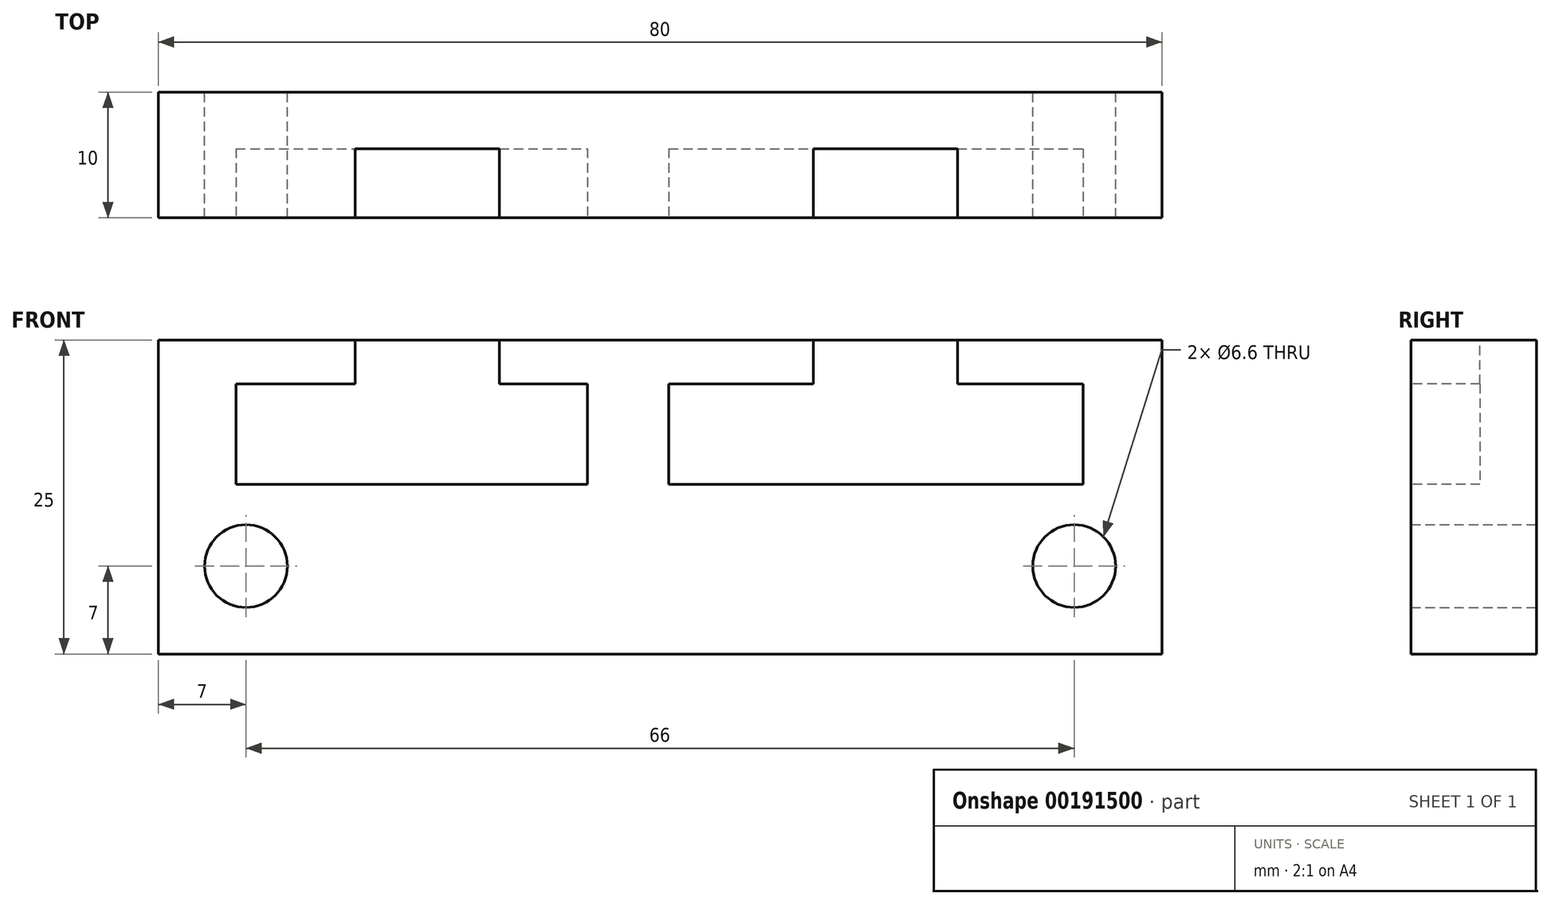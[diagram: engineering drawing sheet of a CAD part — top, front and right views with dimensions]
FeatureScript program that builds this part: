
annotation { "Feature Type Name" : "Feature", "Feature Type Description" : "" }
export const myFeature = defineFeature(function(context is Context, id is Id, definition is map)
    precondition{}
    {
        {
            var Q0;
            Q0=qCreatedBy(makeId("Front.planeOp"),FACE);
            var sketch = newSketch(context, id + "F0", { "sketchPlane" : qUnion([Q0])});
            skLineSegment(sketch, "E0.bottom", {"start": v(0, 0) * mm, "end": v(80, 0) * mm});
            skLineSegment(sketch, "E0.top", {"start": v(0, 25) * mm, "end": v(80, 25) * mm});
            skLineSegment(sketch, "E0.left", {"start": v(0, 0) * mm, "end": v(0, 25) * mm});
            skLineSegment(sketch, "E0.right", {"start": v(80, 0) * mm, "end": v(80, 25) * mm});
            skLineSegment(sketch, "E1.bottom", {"start": v(0, 0) * mm, "end": v(7, 0) * mm, "construction": true});
            skLineSegment(sketch, "E1.top", {"start": v(0, 7) * mm, "end": v(7, 7) * mm, "construction": true});
            skLineSegment(sketch, "E1.left", {"start": v(0, 0) * mm, "end": v(0, 7) * mm, "construction": true});
            skLineSegment(sketch, "E1.right", {"start": v(7, 0) * mm, "end": v(7, 7) * mm, "construction": true});
            skLineSegment(sketch, "E2.bottom", {"start": v(80, 0) * mm, "end": v(73, 0) * mm, "construction": true});
            skLineSegment(sketch, "E2.top", {"start": v(80, 7) * mm, "end": v(73, 7) * mm, "construction": true});
            skLineSegment(sketch, "E2.left", {"start": v(80, 0) * mm, "end": v(80, 7) * mm, "construction": true});
            skLineSegment(sketch, "E2.right", {"start": v(73, 0) * mm, "end": v(73, 7) * mm, "construction": true});
            skCircle(sketch, "E3", {"center": v(7, 7) * mm, "radius": 3.3 * mm});
            skCircle(sketch, "E4", {"center": v(73, 7) * mm, "radius": 3.3 * mm});
            skSolve(sketch);
        }
        {
            var Q0;
            Q0=makeQuery(id+"F0.imprint","IMPRINT",FACE,{"disambiguationData":[TD([[makeQuery(id+"F0.imprint","IMPRINT",EDGE,{"derivedFrom":sQuery(id+"F0.wireOp",EDGE,"E0.bottom")}),1.0]])]});
            extrude(context, id + "F1", {"entities" : qUnion([Q0]), "depth" : 10 * mm});
        }
        {
            var Q0;
            Q0=makeQuery(id+"F1.opExtrude","CAP_FACE",FACE,{"disambiguationData":[OSD([sQuery(id+"F0.wireOp",EDGE,"E0.bottom"),sQuery(id+"F0.wireOp",EDGE,"E0.top"),sQuery(id+"F0.wireOp",EDGE,"E0.left"),sQuery(id+"F0.wireOp",EDGE,"E0.right")])],"isStart":false});
            var sketch = newSketch(context, id + "F2", { "sketchPlane" : qUnion([Q0])});
            skPoint(sketch, "E5.bottom.start.orphan", {"position": v(0, 21.5) * mm});
            skPoint(sketch, "E6.end.orphan", {"position": v(80, 21.5) * mm});
            skPoint(sketch, "E7.start.orphan", {"position": v(16.7, 21.5) * mm});
            skPoint(sketch, "E8.start.orphan", {"position": v(28.2, 21.5) * mm});
            skPoint(sketch, "E9.end.orphan", {"position": v(55.3, 21.5) * mm});
            skPoint(sketch, "E10.start.orphan", {"position": v(66.8, 21.5) * mm});
            skLineSegment(sketch, "E11", {"start": v(0, 21.5) * mm, "end": v(6.2, 21.5) * mm, "construction": true});
            skLineSegment(sketch, "E12", {"start": v(6.2, 21.5) * mm, "end": v(15.7, 21.5) * mm});
            skLineSegment(sketch, "E13", {"start": v(15.7, 21.5) * mm, "end": v(15.7, 25) * mm});
            skLineSegment(sketch, "E14", {"start": v(15.7, 25) * mm, "end": v(27.2, 25) * mm});
            skLineSegment(sketch, "E15", {"start": v(27.2, 25) * mm, "end": v(27.2, 21.5) * mm});
            skLineSegment(sketch, "E16", {"start": v(27.2, 21.5) * mm, "end": v(34.2, 21.5) * mm});
            skLineSegment(sketch, "E17", {"start": v(34.2, 21.5) * mm, "end": v(40.7, 21.5) * mm, "construction": true});
            skLineSegment(sketch, "E18", {"start": v(40.7, 21.5) * mm, "end": v(52.2, 21.5) * mm});
            skLineSegment(sketch, "E19", {"start": v(52.2, 21.5) * mm, "end": v(52.2, 25) * mm});
            skLineSegment(sketch, "E20", {"start": v(52.2, 25) * mm, "end": v(63.7, 25) * mm});
            skLineSegment(sketch, "E21", {"start": v(63.7, 25) * mm, "end": v(63.7, 21.5) * mm});
            skLineSegment(sketch, "E22", {"start": v(63.7, 21.5) * mm, "end": v(73.7, 21.5) * mm});
            skLineSegment(sketch, "E23", {"start": v(6.2, 21.5) * mm, "end": v(6.2, 13.5) * mm});
            skLineSegment(sketch, "E24", {"start": v(6.2, 13.5) * mm, "end": v(34.2, 13.5) * mm});
            skLineSegment(sketch, "E25", {"start": v(34.2, 13.5) * mm, "end": v(34.2, 21.5) * mm});
            skLineSegment(sketch, "E26", {"start": v(40.7, 21.5) * mm, "end": v(40.7, 13.5) * mm});
            skLineSegment(sketch, "E27", {"start": v(40.7, 13.5) * mm, "end": v(73.7, 13.5) * mm});
            skLineSegment(sketch, "E28", {"start": v(73.7, 13.5) * mm, "end": v(73.7, 21.5) * mm});
            skSolve(sketch);
        }
        {
            var Q0;
            Q0=makeQuery(id+"F2.imprint","IMPRINT",FACE,{"disambiguationData":[TD([[makeQuery(id+"F2.imprint","IMPRINT",EDGE,{"derivedFrom":sQuery(id+"F2.wireOp",EDGE,"E12")}),-1.0]])]});
            var Q1;
            Q1=makeQuery(id+"F2.imprint","IMPRINT",FACE,{"disambiguationData":[TD([[makeQuery(id+"F2.imprint","IMPRINT",EDGE,{"derivedFrom":sQuery(id+"F2.wireOp",EDGE,"E18")}),-1.0]])]});
            extrude(context, id + "F3", {"entities" : qUnion([Q0, Q1]), "operationType" : NewBodyOperationType.REMOVE, "oppositeDirection" : true, "depth" : 5.5 * mm});
        }
    });
